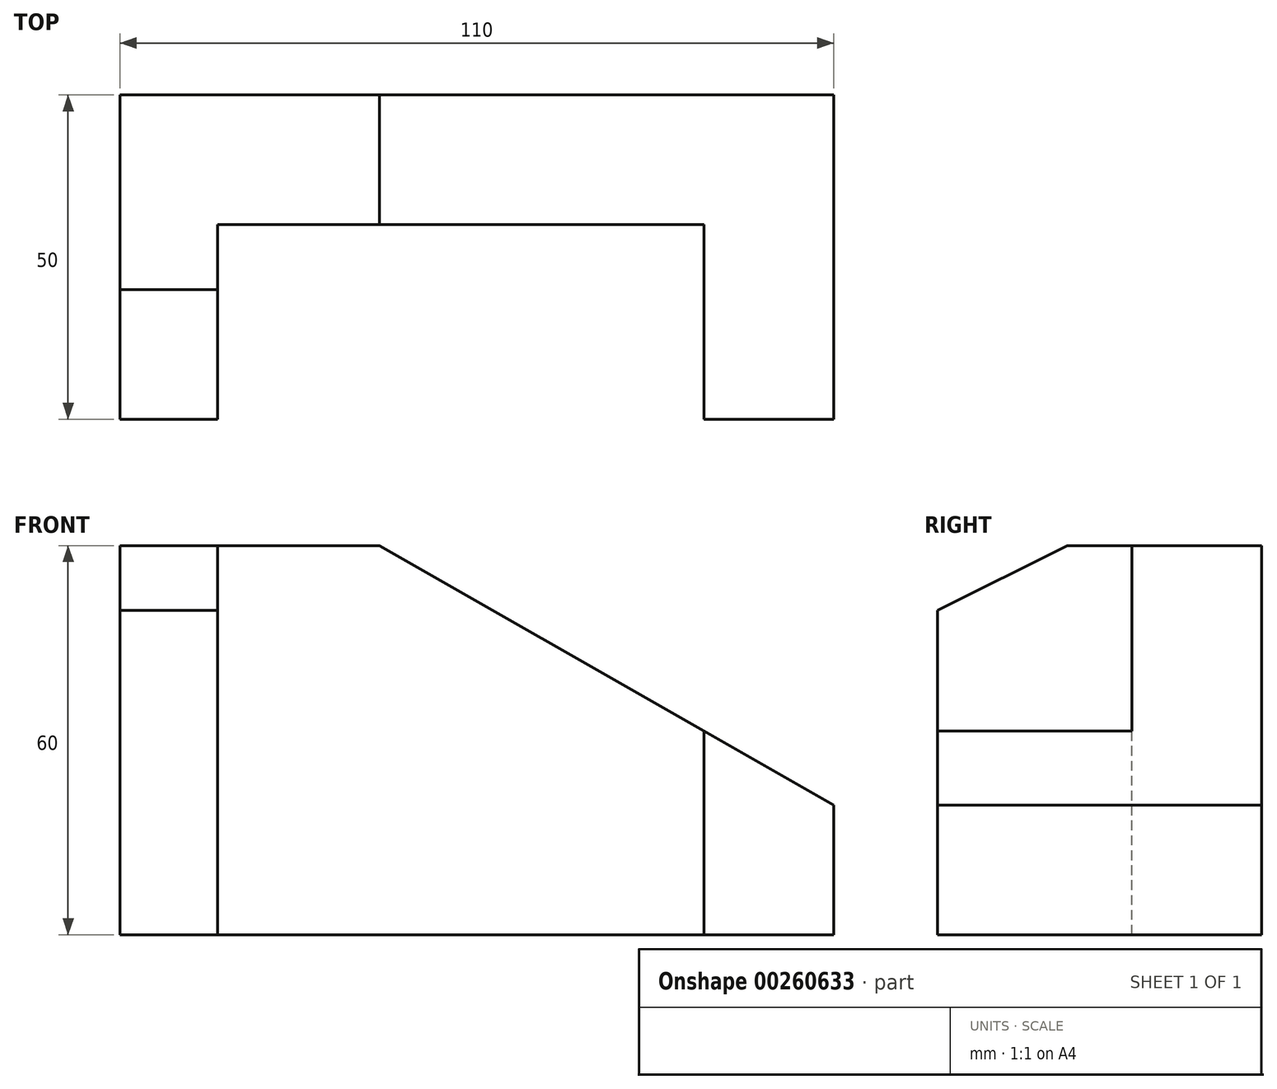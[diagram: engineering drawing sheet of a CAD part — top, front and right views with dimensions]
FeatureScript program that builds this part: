
annotation { "Feature Type Name" : "Feature", "Feature Type Description" : "" }
export const myFeature = defineFeature(function(context is Context, id is Id, definition is map)
    precondition{}
    {
        {
            assignVariable(context, id + "F0", {"name" : "B", "anyValue" : 60});
        }
        {
            assignVariable(context, id + "F1", {"name" : "C", "anyValue" : 50});
        }
        {
            var Q0;
            Q0=qCreatedBy(makeId("Top.planeOp"),FACE);
            var sketch = newSketch(context, id + "F2", { "sketchPlane" : qUnion([Q0])});
            skLineSegment(sketch, "E0.bottom", {"start": v(55, -25) * mm, "end": v(-55, -25) * mm});
            skLineSegment(sketch, "E0.top", {"start": v(55, 25) * mm, "end": v(-55, 25) * mm});
            skLineSegment(sketch, "E0.left", {"start": v(55, -25) * mm, "end": v(55, 25) * mm});
            skLineSegment(sketch, "E0.right", {"start": v(-55, -25) * mm, "end": v(-55, 25) * mm});
            skPoint(sketch, "E0.middle", {"position": v(0, 0) * mm});
            skSolve(sketch);
        }
        {
            var Q0;
            Q0 = qSketchRegion(id + "F2", true);
            extrude(context, id + "F3", {"entities" : qUnion([Q0]), "endBound" : BoundingType.SYMMETRIC, "depth" : (getVariable(context, 'B')) * mm});
        }
        {
            var Q0;
            Q0=makeQuery(id+"F3.opExtrude","SWEPT_FACE",FACE,{"disambiguationData":[OSD([sQuery(id+"F2.wireOp",EDGE,"E0.bottom")])]});
            var sketch = newSketch(context, id + "F4", { "sketchPlane" : qUnion([Q0])});
            skLineSegment(sketch, "E1.bottom", {"start": v(-40, -30) * mm, "end": v(35, -30) * mm});
            skLineSegment(sketch, "E1.top", {"start": v(-40, 30) * mm, "end": v(35, 30) * mm});
            skLineSegment(sketch, "E1.left", {"start": v(-40, -30) * mm, "end": v(-40, 30) * mm});
            skLineSegment(sketch, "E1.right", {"start": v(35, -30) * mm, "end": v(35, 30) * mm});
            skSolve(sketch);
        }
        {
            var Q0;
            Q0 = qSketchRegion(id + "F4", true);
            extrude(context, id + "F5", {"entities" : qUnion([Q0]), "operationType" : NewBodyOperationType.REMOVE, "oppositeDirection" : true, "depth" : 30 * mm});
        }
        {
            var Q0;
            Q0=makeQuery(id+"F3.opExtrude","SWEPT_FACE",FACE,{"disambiguationData":[OSD([sQuery(id+"F2.wireOp",EDGE,"E0.top")])]});
            var sketch = newSketch(context, id + "F6", { "sketchPlane" : qUnion([Q0])});
            skLineSegment(sketch, "E2", {"start": v(15, 30) * mm, "end": v(-55, -10) * mm});
            skLineSegment(sketch, "E3", {"start": v(-55, -10) * mm, "end": v(-55, 30) * mm});
            skLineSegment(sketch, "E4", {"start": v(-55, 30) * mm, "end": v(15, 30) * mm});
            skSolve(sketch);
        }
        {
            var Q0;
            Q0 = qSketchRegion(id + "F6", true);
            extrude(context, id + "F7", {"entities" : qUnion([Q0]), "operationType" : NewBodyOperationType.REMOVE, "oppositeDirection" : true, "depth" : (getVariable(context, 'B')) * mm});
        }
        {
            var Q0;
            Q0=makeQuery(id+"F3.opExtrude","SWEPT_FACE",FACE,{"disambiguationData":[OSD([sQuery(id+"F2.wireOp",EDGE,"E0.right")])]});
            var sketch = newSketch(context, id + "F8", { "sketchPlane" : qUnion([Q0])});
            skLineSegment(sketch, "E5", {"start": v(5, 30) * mm, "end": v(25, 20) * mm});
            skLineSegment(sketch, "E6", {"start": v(25, 20) * mm, "end": v(25, 30) * mm});
            skLineSegment(sketch, "E7", {"start": v(25, 30) * mm, "end": v(5, 30) * mm});
            skSolve(sketch);
        }
        {
            var Q0;
            Q0 = qSketchRegion(id + "F8", true);
            extrude(context, id + "F9", {"entities" : qUnion([Q0]), "operationType" : NewBodyOperationType.REMOVE, "oppositeDirection" : true, "depth" : (getVariable(context, 'C')) * mm});
        }
    });
